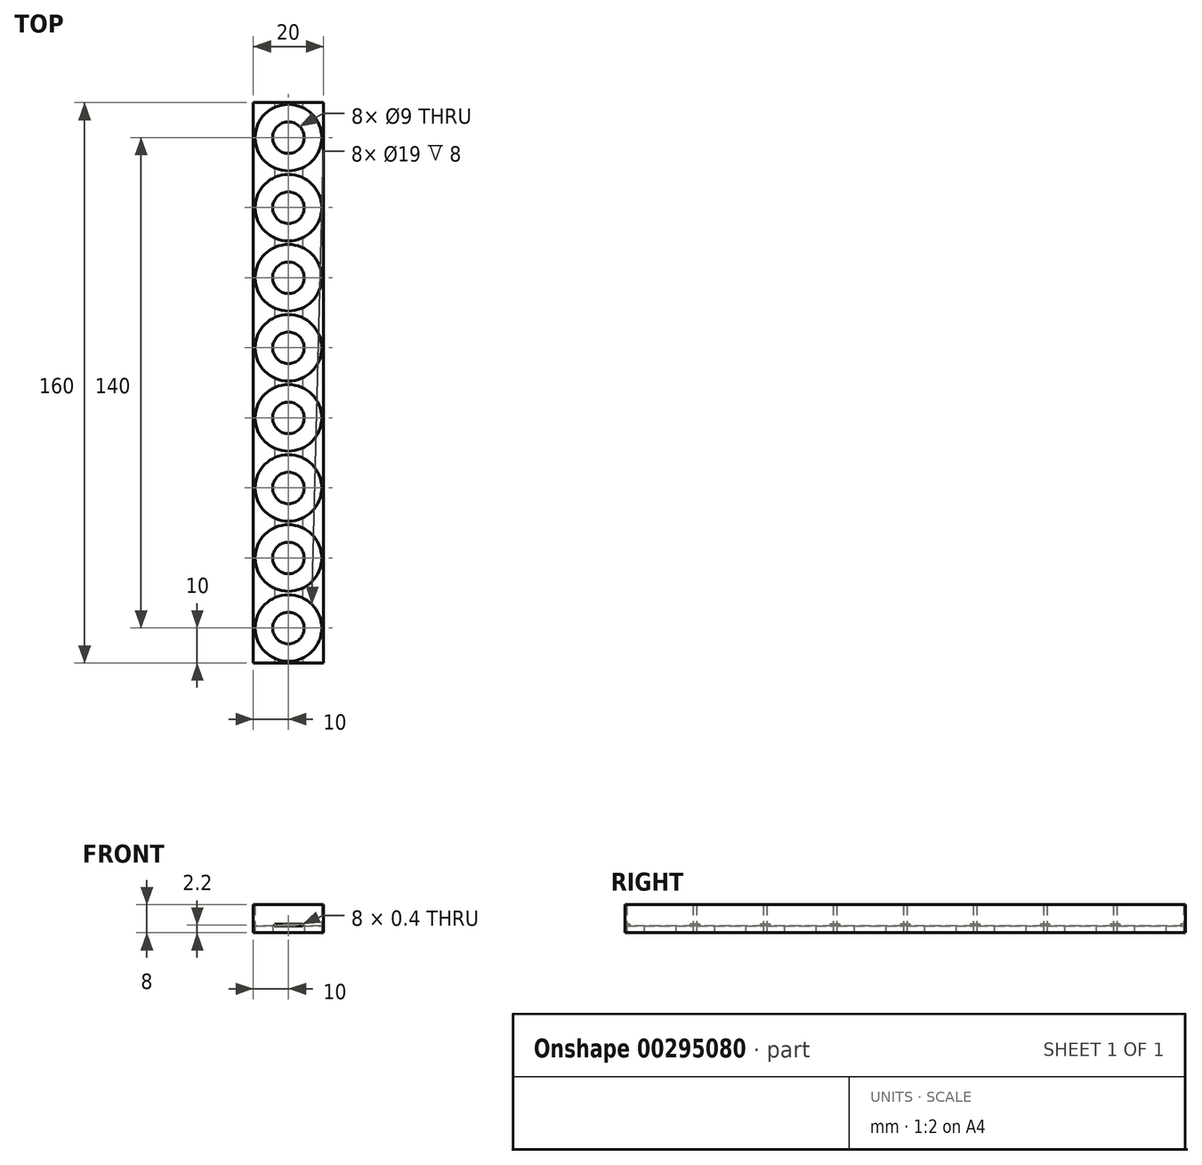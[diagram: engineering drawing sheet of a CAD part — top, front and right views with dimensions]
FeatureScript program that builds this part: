
annotation { "Feature Type Name" : "Feature", "Feature Type Description" : "" }
export const myFeature = defineFeature(function(context is Context, id is Id, definition is map)
    precondition{}
    {
        {
            var Q0;
            Q0=qCreatedBy(makeId("Top.planeOp"),FACE);
            var sketch = newSketch(context, id + "F0", { "sketchPlane" : qUnion([Q0])});
            skLineSegment(sketch, "E0.bottom", {"start": v(-10, 10) * mm, "end": v(10, 10) * mm});
            skLineSegment(sketch, "E0.top", {"start": v(-10, -10) * mm, "end": v(10, -10) * mm});
            skLineSegment(sketch, "E0.left", {"start": v(-10, 10) * mm, "end": v(-10, -10) * mm});
            skLineSegment(sketch, "E0.right", {"start": v(10, 10) * mm, "end": v(10, -10) * mm});
            skPoint(sketch, "E0.middle", {"position": v(0, 0) * mm});
            skCircle(sketch, "E1", {"center": v(0, 0) * mm, "radius": 9.5 * mm});
            skCircle(sketch, "E2", {"center": v(0, 0) * mm, "radius": 4.5 * mm});
            skLineSegment(sketch, "E3.0.1.0", {"start": v(-10, 30) * mm, "end": v(-10, 10) * mm});
            skCircle(sketch, "E3.0.1.2", {"center": v(0, 20) * mm, "radius": 4.5 * mm});
            skLineSegment(sketch, "E3.0.1.3", {"start": v(-10, 30) * mm, "end": v(10, 30) * mm});
            skPoint(sketch, "E3.0.1.4", {"position": v(0, 20) * mm});
            skCircle(sketch, "E3.0.1.5", {"center": v(0, 20) * mm, "radius": 9.5 * mm});
            skLineSegment(sketch, "E3.0.1.6", {"start": v(10, 30) * mm, "end": v(10, 10) * mm});
            skLineSegment(sketch, "E3.0.2.0", {"start": v(-10, 50) * mm, "end": v(-10, 30) * mm});
            skLineSegment(sketch, "E3.0.2.1", {"start": v(-10, 30) * mm, "end": v(10, 30) * mm});
            skCircle(sketch, "E3.0.2.2", {"center": v(0, 40) * mm, "radius": 4.5 * mm});
            skLineSegment(sketch, "E3.0.2.3", {"start": v(-10, 50) * mm, "end": v(10, 50) * mm});
            skPoint(sketch, "E3.0.2.4", {"position": v(0, 40) * mm});
            skCircle(sketch, "E3.0.2.5", {"center": v(0, 40) * mm, "radius": 9.5 * mm});
            skLineSegment(sketch, "E3.0.2.6", {"start": v(10, 50) * mm, "end": v(10, 30) * mm});
            skLineSegment(sketch, "E3.0.3.0", {"start": v(-10, 70) * mm, "end": v(-10, 50) * mm});
            skLineSegment(sketch, "E3.0.3.1", {"start": v(-10, 50) * mm, "end": v(10, 50) * mm});
            skCircle(sketch, "E3.0.3.2", {"center": v(0, 60) * mm, "radius": 4.5 * mm});
            skLineSegment(sketch, "E3.0.3.3", {"start": v(-10, 70) * mm, "end": v(10, 70) * mm});
            skPoint(sketch, "E3.0.3.4", {"position": v(0, 60) * mm});
            skCircle(sketch, "E3.0.3.5", {"center": v(0, 60) * mm, "radius": 9.5 * mm});
            skLineSegment(sketch, "E3.0.3.6", {"start": v(10, 70) * mm, "end": v(10, 50) * mm});
            skLineSegment(sketch, "E3.0.4.0", {"start": v(-10, 90) * mm, "end": v(-10, 70) * mm});
            skLineSegment(sketch, "E3.0.4.1", {"start": v(-10, 70) * mm, "end": v(10, 70) * mm});
            skCircle(sketch, "E3.0.4.2", {"center": v(0, 80) * mm, "radius": 4.5 * mm});
            skLineSegment(sketch, "E3.0.4.3", {"start": v(-10, 90) * mm, "end": v(10, 90) * mm});
            skPoint(sketch, "E3.0.4.4", {"position": v(0, 80) * mm});
            skCircle(sketch, "E3.0.4.5", {"center": v(0, 80) * mm, "radius": 9.5 * mm});
            skLineSegment(sketch, "E3.0.4.6", {"start": v(10, 90) * mm, "end": v(10, 70) * mm});
            skLineSegment(sketch, "E3.0.5.0", {"start": v(-10, 110) * mm, "end": v(-10, 90) * mm});
            skLineSegment(sketch, "E3.0.5.1", {"start": v(-10, 90) * mm, "end": v(10, 90) * mm});
            skCircle(sketch, "E3.0.5.2", {"center": v(0, 100) * mm, "radius": 4.5 * mm});
            skLineSegment(sketch, "E3.0.5.3", {"start": v(-10, 110) * mm, "end": v(10, 110) * mm});
            skPoint(sketch, "E3.0.5.4", {"position": v(0, 100) * mm});
            skCircle(sketch, "E3.0.5.5", {"center": v(0, 100) * mm, "radius": 9.5 * mm});
            skLineSegment(sketch, "E3.0.5.6", {"start": v(10, 110) * mm, "end": v(10, 90) * mm});
            skLineSegment(sketch, "E3.0.6.0", {"start": v(-10, 130) * mm, "end": v(-10, 110) * mm});
            skLineSegment(sketch, "E3.0.6.1", {"start": v(-10, 110) * mm, "end": v(10, 110) * mm});
            skCircle(sketch, "E3.0.6.2", {"center": v(0, 120) * mm, "radius": 4.5 * mm});
            skLineSegment(sketch, "E3.0.6.3", {"start": v(-10, 130) * mm, "end": v(10, 130) * mm});
            skPoint(sketch, "E3.0.6.4", {"position": v(0, 120) * mm});
            skCircle(sketch, "E3.0.6.5", {"center": v(0, 120) * mm, "radius": 9.5 * mm});
            skLineSegment(sketch, "E3.0.6.6", {"start": v(10, 130) * mm, "end": v(10, 110) * mm});
            skLineSegment(sketch, "E3.0.7.0", {"start": v(-10, 150) * mm, "end": v(-10, 130) * mm});
            skLineSegment(sketch, "E3.0.7.1", {"start": v(-10, 130) * mm, "end": v(10, 130) * mm});
            skCircle(sketch, "E3.0.7.2", {"center": v(0, 140) * mm, "radius": 4.5 * mm});
            skLineSegment(sketch, "E3.0.7.3", {"start": v(-10, 150) * mm, "end": v(10, 150) * mm});
            skPoint(sketch, "E3.0.7.4", {"position": v(0, 140) * mm});
            skCircle(sketch, "E3.0.7.5", {"center": v(0, 140) * mm, "radius": 9.5 * mm});
            skLineSegment(sketch, "E3.0.7.6", {"start": v(10, 150) * mm, "end": v(10, 130) * mm});
            skLineSegment(sketch, "E3.direction1", {"start": v(-10, -10) * mm, "end": v(10, -10) * mm, "construction": true});
            skLineSegment(sketch, "E3.direction2", {"start": v(-10, -10) * mm, "end": v(-10, 10) * mm, "construction": true});
            skSolve(sketch);
        }
        {
            var Q0;
            Q0=makeQuery(id+"F0.imprint","IMPRINT",FACE,{"disambiguationData":[TD([[makeQuery(id+"F0.imprint","IMPRINT",EDGE,{"derivedFrom":sQuery(id+"F0.wireOp",EDGE,"E1")}),1.0]])]});
            var Q1;
            Q1=makeQuery(id+"F0.imprint","IMPRINT",FACE,{"disambiguationData":[TD([[makeQuery(id+"F0.imprint","IMPRINT",EDGE,{"derivedFrom":sQuery(id+"F0.wireOp",EDGE,"E3.0.1.2")}),-1.0]])]});
            var Q2;
            Q2=makeQuery(id+"F0.imprint","IMPRINT",FACE,{"disambiguationData":[TD([[makeQuery(id+"F0.imprint","IMPRINT",EDGE,{"derivedFrom":sQuery(id+"F0.wireOp",EDGE,"E3.0.2.2")}),-1.0]])]});
            var Q3;
            Q3=makeQuery(id+"F0.imprint","IMPRINT",FACE,{"disambiguationData":[TD([[makeQuery(id+"F0.imprint","IMPRINT",EDGE,{"derivedFrom":sQuery(id+"F0.wireOp",EDGE,"E3.0.3.2")}),-1.0]])]});
            var Q4;
            Q4=makeQuery(id+"F0.imprint","IMPRINT",FACE,{"disambiguationData":[TD([[makeQuery(id+"F0.imprint","IMPRINT",EDGE,{"derivedFrom":sQuery(id+"F0.wireOp",EDGE,"E3.0.4.2")}),-1.0]])]});
            var Q5;
            Q5=makeQuery(id+"F0.imprint","IMPRINT",FACE,{"disambiguationData":[TD([[makeQuery(id+"F0.imprint","IMPRINT",EDGE,{"derivedFrom":sQuery(id+"F0.wireOp",EDGE,"E3.0.5.2")}),-1.0]])]});
            var Q6;
            Q6=makeQuery(id+"F0.imprint","IMPRINT",FACE,{"disambiguationData":[TD([[makeQuery(id+"F0.imprint","IMPRINT",EDGE,{"derivedFrom":sQuery(id+"F0.wireOp",EDGE,"E3.0.6.2")}),-1.0]])]});
            var Q7;
            Q7=makeQuery(id+"F0.imprint","IMPRINT",FACE,{"disambiguationData":[TD([[makeQuery(id+"F0.imprint","IMPRINT",EDGE,{"derivedFrom":sQuery(id+"F0.wireOp",EDGE,"E3.0.7.2")}),-1.0]])]});
            extrude(context, id + "F1", {"entities" : qUnion([Q0, Q1, Q2, Q3, Q4, Q5, Q6, Q7]), "depth" : 2 * mm});
        }
        {
            var Q0;
            Q0=makeQuery(id+"F0.imprint","IMPRINT",FACE,{"disambiguationData":[TD([[makeQuery(id+"F0.imprint","IMPRINT",EDGE,{"derivedFrom":sQuery(id+"F0.wireOp",EDGE,"E0.top")}),1.0]])]});
            var Q1;
            Q1=makeQuery(id+"F0.imprint","IMPRINT",FACE,{"disambiguationData":[TD([[makeQuery(id+"F0.imprint","IMPRINT",EDGE,{"derivedFrom":sQuery(id+"F0.wireOp",EDGE,"E3.0.1.0")}),1.0]])]});
            var Q2;
            Q2=makeQuery(id+"F0.imprint","IMPRINT",FACE,{"disambiguationData":[TD([[makeQuery(id+"F0.imprint","IMPRINT",EDGE,{"derivedFrom":sQuery(id+"F0.wireOp",EDGE,"E3.0.2.0")}),1.0]])]});
            var Q3;
            Q3=makeQuery(id+"F0.imprint","IMPRINT",FACE,{"disambiguationData":[TD([[makeQuery(id+"F0.imprint","IMPRINT",EDGE,{"derivedFrom":sQuery(id+"F0.wireOp",EDGE,"E3.0.3.0")}),1.0]])]});
            var Q4;
            Q4=makeQuery(id+"F0.imprint","IMPRINT",FACE,{"disambiguationData":[TD([[makeQuery(id+"F0.imprint","IMPRINT",EDGE,{"derivedFrom":sQuery(id+"F0.wireOp",EDGE,"E3.0.4.0")}),1.0]])]});
            var Q5;
            Q5=makeQuery(id+"F0.imprint","IMPRINT",FACE,{"disambiguationData":[TD([[makeQuery(id+"F0.imprint","IMPRINT",EDGE,{"derivedFrom":sQuery(id+"F0.wireOp",EDGE,"E3.0.5.0")}),1.0]])]});
            var Q6;
            Q6=makeQuery(id+"F0.imprint","IMPRINT",FACE,{"disambiguationData":[TD([[makeQuery(id+"F0.imprint","IMPRINT",EDGE,{"derivedFrom":sQuery(id+"F0.wireOp",EDGE,"E3.0.6.0")}),1.0]])]});
            var Q7;
            Q7=makeQuery(id+"F0.imprint","IMPRINT",FACE,{"disambiguationData":[TD([[makeQuery(id+"F0.imprint","IMPRINT",EDGE,{"derivedFrom":sQuery(id+"F0.wireOp",EDGE,"E3.0.7.0")}),1.0]])]});
            extrude(context, id + "F2", {"entities" : qUnion([Q0, Q1, Q2, Q3, Q4, Q5, Q6, Q7]), "depth" : 8 * mm});
        }
        {
            var Q0;
            Q0=makeQuery(id+"F2.opExtrude","SWEPT_FACE",FACE,{"disambiguationData":[OSD([sQuery(id+"F0.wireOp",EDGE,"E0.top")])]});
            var sketch = newSketch(context, id + "F3", { "sketchPlane" : qUnion([Q0])});
            skLineSegment(sketch, "E4.bottom", {"start": v(-4, 2.4) * mm, "end": v(4, 2.4) * mm});
            skLineSegment(sketch, "E4.top", {"start": v(-4, 2) * mm, "end": v(4, 2) * mm});
            skLineSegment(sketch, "E4.left", {"start": v(-4, 2.4) * mm, "end": v(-4, 2) * mm});
            skLineSegment(sketch, "E4.right", {"start": v(4, 2.4) * mm, "end": v(4, 2) * mm});
            skSolve(sketch);
        }
        {
            var Q0;
            Q0=makeQuery(id+"F3.imprint","IMPRINT",FACE,{"disambiguationData":[TD([[makeQuery(id+"F3.imprint","IMPRINT",EDGE,{"derivedFrom":sQuery(id+"F3.wireOp",EDGE,"E4.bottom")}),-1.0]])]});
            extrude(context, id + "F4", {"entities" : qUnion([Q0]), "operationType" : NewBodyOperationType.REMOVE, "endBound" : BoundingType.THROUGH_ALL, "oppositeDirection" : true, "depth" : 25 * mm});
        }
    });
